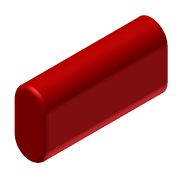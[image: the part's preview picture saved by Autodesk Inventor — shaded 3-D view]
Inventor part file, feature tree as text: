
AUTODESK INVENTOR PART (.ipt)
format: ipt  version: 2014 (Build 180170000, 170)  size: 84,992 bytes
history: native  units: mm (DEFAULTED — no unit token found)
features: extrude x1, fillet x1, sketch x1, reference x1
ambient origin geometry x8: Origin, YZ Plane, XZ Plane, XY Plane, X Axis, Y Axis, Z Axis, Center Point
bodies: Solid1 (feature_tree)
feature tree (4):
  extrude  "Extrusion1"  Depth=0.381mm
  fillet  "Fillet1"  [1 undecoded]
  sketch  "Sketch1"  dims[d0=12.7mm d1=0.0mm d2=0.381mm]
  reference  "Reference1"
note: 1 required parameter value undecoded (feature->parameter linkage not recoverable at this tier; creation-order binding heuristic only, values carry confidence <= 0.55)
